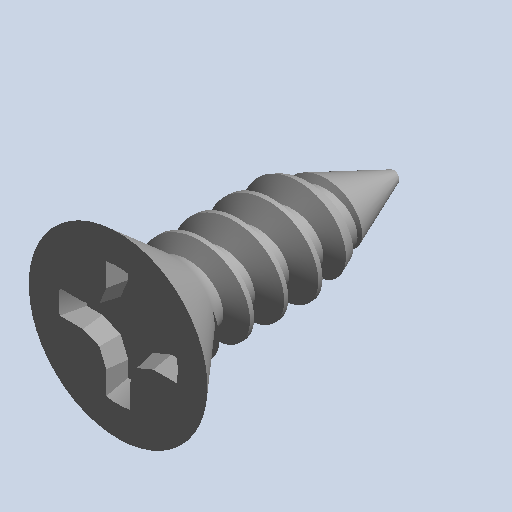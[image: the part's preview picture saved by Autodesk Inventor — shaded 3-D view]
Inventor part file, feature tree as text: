
AUTODESK INVENTOR PART (.ipt)
format: ipt  version: 2022.1 (Build 261234000, 234)  size: 313,344 bytes
history: native  units: mm (DEFAULTED — no unit token found)
features: other x8, revolve x1
bodies: Body1 (feature_tree)
feature tree (9):
  other  "Sólido1"
  other  "Origen"
  other  "Plano YZ"
  other  "Plano XZ"
  other  "Plano XY"
  other  "Eje X"
  other  "Eje Y"
  other  "Eje Z"
  revolve  "Revolve2"  [1 undecoded]
note: 1 required parameter value undecoded (feature->parameter linkage not recoverable at this tier; creation-order binding heuristic only, values carry confidence <= 0.55)
